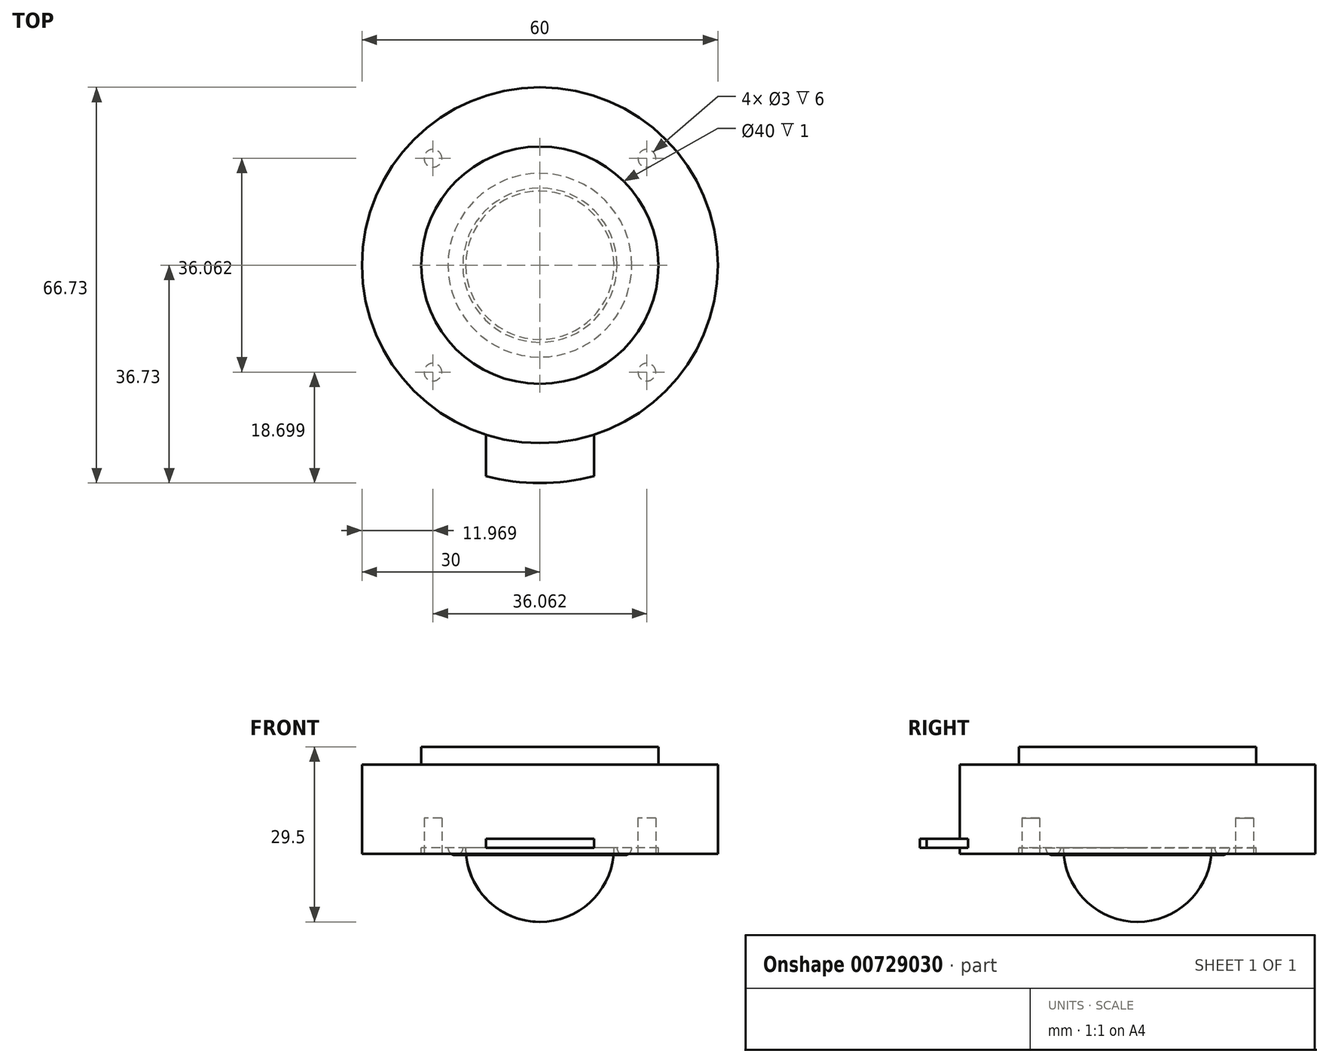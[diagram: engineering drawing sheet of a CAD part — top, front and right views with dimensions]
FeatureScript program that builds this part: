
annotation { "Feature Type Name" : "Feature", "Feature Type Description" : "" }
export const myFeature = defineFeature(function(context is Context, id is Id, definition is map)
    precondition{}
    {
        {
            var Q0;
            Q0=qCreatedBy(makeId("Top.planeOp"),FACE);
            var sketch = newSketch(context, id + "F0", { "sketchPlane" : qUnion([Q0])});
            skCircle(sketch, "E0", {"center": v(0, 0) * mm, "radius": 30 * mm});
            skCircle(sketch, "E1", {"center": v(0, 0) * mm, "radius": 12.5 * mm});
            skCircle(sketch, "E2", {"center": v(0, 0) * mm, "radius": 27 * mm});
            skLineSegment(sketch, "E3", {"start": v(-9.12, -28.58) * mm, "end": v(-9.12, -35.58) * mm});
            skLineSegment(sketch, "E4", {"start": v(9.12, -28.58) * mm, "end": v(9.12, -35.58) * mm});
            skArc(sketch, "E5", {"start": v(-9.12, -35.58) * mm, "mid": v(0, -36.73) * mm, "end": v(9.12, -35.58) * mm});
            skArc(sketch, "E6", {"start": v(-9.12, -32.08) * mm, "mid": v(0, -33.35) * mm, "end": v(9.12, -32.08) * mm, "construction": true});
            skCircle(sketch, "E7", {"center": v(-4.24, -33.08) * mm, "radius": 1 * mm});
            skCircle(sketch, "E8", {"center": v(4.24, -33.08) * mm, "radius": 1 * mm});
            skLineSegment(sketch, "E9", {"start": v(0, 0) * mm, "end": v(-30.2, 30.2) * mm, "construction": true});
            skLineSegment(sketch, "E10", {"start": v(0, 0) * mm, "end": v(29.17, 29.17) * mm, "construction": true});
            skLineSegment(sketch, "E11", {"start": v(0, 0) * mm, "end": v(31.33, -31.33) * mm, "construction": true});
            skLineSegment(sketch, "E12", {"start": v(0, 0) * mm, "end": v(-31.33, -31.33) * mm, "construction": true});
            skCircle(sketch, "E13", {"center": v(-18.03, 18.03) * mm, "radius": 1.5 * mm});
            skCircle(sketch, "E14", {"center": v(18.03, 18.03) * mm, "radius": 1.5 * mm});
            skCircle(sketch, "E15", {"center": v(18.03, -18.03) * mm, "radius": 1.5 * mm});
            skCircle(sketch, "E16", {"center": v(-18.03, -18.03) * mm, "radius": 1.5 * mm});
            skCircle(sketch, "E17", {"center": v(0, 0) * mm, "radius": 20 * mm});
            skSolve(sketch);
        }
        {
            var Q0;
            {var subQ4=sQuery(id+"F0.wireOp",EDGE,"E0");var subQ5=makeQuery(id+"F0.imprint","INTERSECT",VERTEX,{"derivedFrom":[subQ4,sQuery(id+"F0.wireOp",EDGE,"E3")]});Q0=makeQuery(id+"F0.imprint","IMPRINT",FACE,{"disambiguationData":[TD([[makeQuery(id+"F0.imprint","IMPRINT",EDGE,{"disambiguationData":[TD([[subQ5,-1.0]])],"derivedFrom":subQ4}),1.0]])]});}
            var Q1;
            Q1=makeQuery(id+"F0.imprint","IMPRINT",FACE,{"disambiguationData":[TD([[makeQuery(id+"F0.imprint","IMPRINT",EDGE,{"derivedFrom":sQuery(id+"F0.wireOp",EDGE,"E1")}),-1.0]])]});
            var Q2;
            Q2=makeQuery(id+"F0.imprint","IMPRINT",FACE,{"disambiguationData":[TD([[makeQuery(id+"F0.imprint","IMPRINT",EDGE,{"derivedFrom":sQuery(id+"F0.wireOp",EDGE,"E1")}),1.0]])]});
            var Q3;
            Q3=makeQuery(id+"F0.imprint","IMPRINT",FACE,{"disambiguationData":[TD([[makeQuery(id+"F0.imprint","IMPRINT",EDGE,{"derivedFrom":sQuery(id+"F0.wireOp",EDGE,"E14")}),1.0]])]});
            var Q4;
            Q4=makeQuery(id+"F0.imprint","IMPRINT",FACE,{"disambiguationData":[TD([[makeQuery(id+"F0.imprint","IMPRINT",EDGE,{"derivedFrom":sQuery(id+"F0.wireOp",EDGE,"E13")}),1.0]])]});
            var Q5;
            Q5=makeQuery(id+"F0.imprint","IMPRINT",FACE,{"disambiguationData":[TD([[makeQuery(id+"F0.imprint","IMPRINT",EDGE,{"derivedFrom":sQuery(id+"F0.wireOp",EDGE,"E16")}),1.0]])]});
            var Q6;
            Q6=makeQuery(id+"F0.imprint","IMPRINT",FACE,{"disambiguationData":[TD([[makeQuery(id+"F0.imprint","IMPRINT",EDGE,{"derivedFrom":sQuery(id+"F0.wireOp",EDGE,"E15")}),1.0]])]});
            var Q7;
            {var subQ7=sQuery(id+"F0.wireOp",EDGE,"E13");Q7=makeQuery(id+"F0.imprint","IMPRINT",FACE,{"disambiguationData":[TD([[makeQuery(id+"F0.imprint","IMPRINT",EDGE,{"derivedFrom":subQ7}),-1.0]])]});}
            extrude(context, id + "F1", {"entities" : qUnion([Q0, Q1, Q2, Q3, Q4, Q5, Q6, Q7]), "depth" : 14 * mm, "offsetDistance" : 25 * mm});
        }
        {
            var Q0;
            Q0=makeQuery(id+"F0.imprint","IMPRINT",FACE,{"disambiguationData":[TD([[makeQuery(id+"F0.imprint","IMPRINT",EDGE,{"derivedFrom":sQuery(id+"F0.wireOp",EDGE,"E1")}),-1.0]])]});
            var Q1;
            Q1=makeQuery(id+"F0.imprint","IMPRINT",FACE,{"disambiguationData":[TD([[makeQuery(id+"F0.imprint","IMPRINT",EDGE,{"derivedFrom":sQuery(id+"F0.wireOp",EDGE,"E1")}),1.0]])]});
            extrude(context, id + "F2", {"entities" : qUnion([Q0, Q1]), "operationType" : NewBodyOperationType.ADD, "depth" : 17 * mm, "offsetDistance" : 25 * mm});
        }
        {
            var Q0;
            {var subQ1=sQuery(id+"F0.wireOp",EDGE,"E3");Q0=makeQuery(id+"F0.imprint","IMPRINT",FACE,{"disambiguationData":[TD([[makeQuery(id+"F0.imprint","IMPRINT",EDGE,{"derivedFrom":subQ1}),1.0]])]});}
            var Q1;
            Q1=makeQuery(id+"F0.imprint","IMPRINT",FACE,{"disambiguationData":[TD([[makeQuery(id+"F0.imprint","IMPRINT",EDGE,{"derivedFrom":sQuery(id+"F0.wireOp",EDGE,"E7")}),1.0]])]});
            var Q2;
            Q2=makeQuery(id+"F0.imprint","IMPRINT",FACE,{"disambiguationData":[TD([[makeQuery(id+"F0.imprint","IMPRINT",EDGE,{"derivedFrom":sQuery(id+"F0.wireOp",EDGE,"E8")}),1.0]])]});
            extrude(context, id + "F3", {"entities" : qUnion([Q0, Q1, Q2]), "operationType" : NewBodyOperationType.ADD, "depth" : 1.5 * mm, "offsetDistance" : 25 * mm});
        }
        {
            var Q0;
            Q0=makeQuery(id+"F0.imprint","IMPRINT",FACE,{"disambiguationData":[TD([[makeQuery(id+"F0.imprint","IMPRINT",EDGE,{"derivedFrom":sQuery(id+"F0.wireOp",EDGE,"E13")}),1.0]])]});
            var Q1;
            Q1=makeQuery(id+"F0.imprint","IMPRINT",FACE,{"disambiguationData":[TD([[makeQuery(id+"F0.imprint","IMPRINT",EDGE,{"derivedFrom":sQuery(id+"F0.wireOp",EDGE,"E14")}),1.0]])]});
            var Q2;
            Q2=makeQuery(id+"F0.imprint","IMPRINT",FACE,{"disambiguationData":[TD([[makeQuery(id+"F0.imprint","IMPRINT",EDGE,{"derivedFrom":sQuery(id+"F0.wireOp",EDGE,"E15")}),1.0]])]});
            var Q3;
            Q3=makeQuery(id+"F0.imprint","IMPRINT",FACE,{"disambiguationData":[TD([[makeQuery(id+"F0.imprint","IMPRINT",EDGE,{"derivedFrom":sQuery(id+"F0.wireOp",EDGE,"E16")}),1.0]])]});
            extrude(context, id + "F4", {"entities" : qUnion([Q0, Q1, Q2, Q3]), "operationType" : NewBodyOperationType.REMOVE, "depth" : 5 * mm, "offsetDistance" : 25 * mm});
        }
        {
            var Q0;
            Q0=qCreatedBy(makeId("Front.planeOp"),FACE);
            var sketch = newSketch(context, id + "F5", { "sketchPlane" : qUnion([Q0])});
            skLineSegment(sketch, "E18", {"start": v(0, 0) * mm, "end": v(0, -14.03) * mm, "construction": true});
            skLineSegment(sketch, "E19.0", {"start": v(0, 0) * mm, "end": v(12.5, 0) * mm});
            skArc(sketch, "E20", {"start": v(12.5, 0) * mm, "mid": v(8.84, -8.84) * mm, "end": v(0, -12.5) * mm});
            skPoint(sketch, "E21.orphan", {"position": v(-12.5, 0) * mm});
            skLineSegment(sketch, "E22", {"start": v(13, 0) * mm, "end": v(14.25, 0) * mm});
            skArc(sketch, "E23", {"start": v(13, 0) * mm, "mid": v(14.25, -1.25) * mm, "end": v(15.5, 0) * mm});
            skLineSegment(sketch, "E24", {"start": v(15.5, 0) * mm, "end": v(14.25, 0) * mm});
            skLineSegment(sketch, "E25", {"start": v(0, -12.5) * mm, "end": v(0, 0) * mm});
            skSolve(sketch);
        }
        {
            var Q0;
            Q0 = qSketchRegion(id + "F5", true);
            var Q1;
            Q1=sQuery(id+"F5.wireOp",EDGE,"E18");
            revolve(context, id + "F6", {"surfaceOperationType" : NewSurfaceOperationType.NEW, "entities" : qUnion([Q0]), "axis" : qUnion([Q1]), "revolveType" : RevolveType.FULL});
        }
        {
            var Q0;
            {var subQ4=sQuery(id+"F0.wireOp",EDGE,"E0");var subQ5=makeQuery(id+"F0.imprint","INTERSECT",VERTEX,{"derivedFrom":[subQ4,sQuery(id+"F0.wireOp",EDGE,"E3")]});Q0=makeQuery(id+"F0.imprint","IMPRINT",FACE,{"disambiguationData":[TD([[makeQuery(id+"F0.imprint","IMPRINT",EDGE,{"disambiguationData":[TD([[subQ5,-1.0]])],"derivedFrom":subQ4}),1.0]])]});}
            var Q1;
            {var subQ7=sQuery(id+"F0.wireOp",EDGE,"E13");Q1=makeQuery(id+"F0.imprint","IMPRINT",FACE,{"disambiguationData":[TD([[makeQuery(id+"F0.imprint","IMPRINT",EDGE,{"derivedFrom":subQ7}),-1.0]])]});}
            extrude(context, id + "F7", {"entities" : qUnion([Q0, Q1]), "operationType" : NewBodyOperationType.ADD, "oppositeDirection" : true, "depth" : 1 * mm, "offsetDistance" : 25 * mm});
        }
    });
